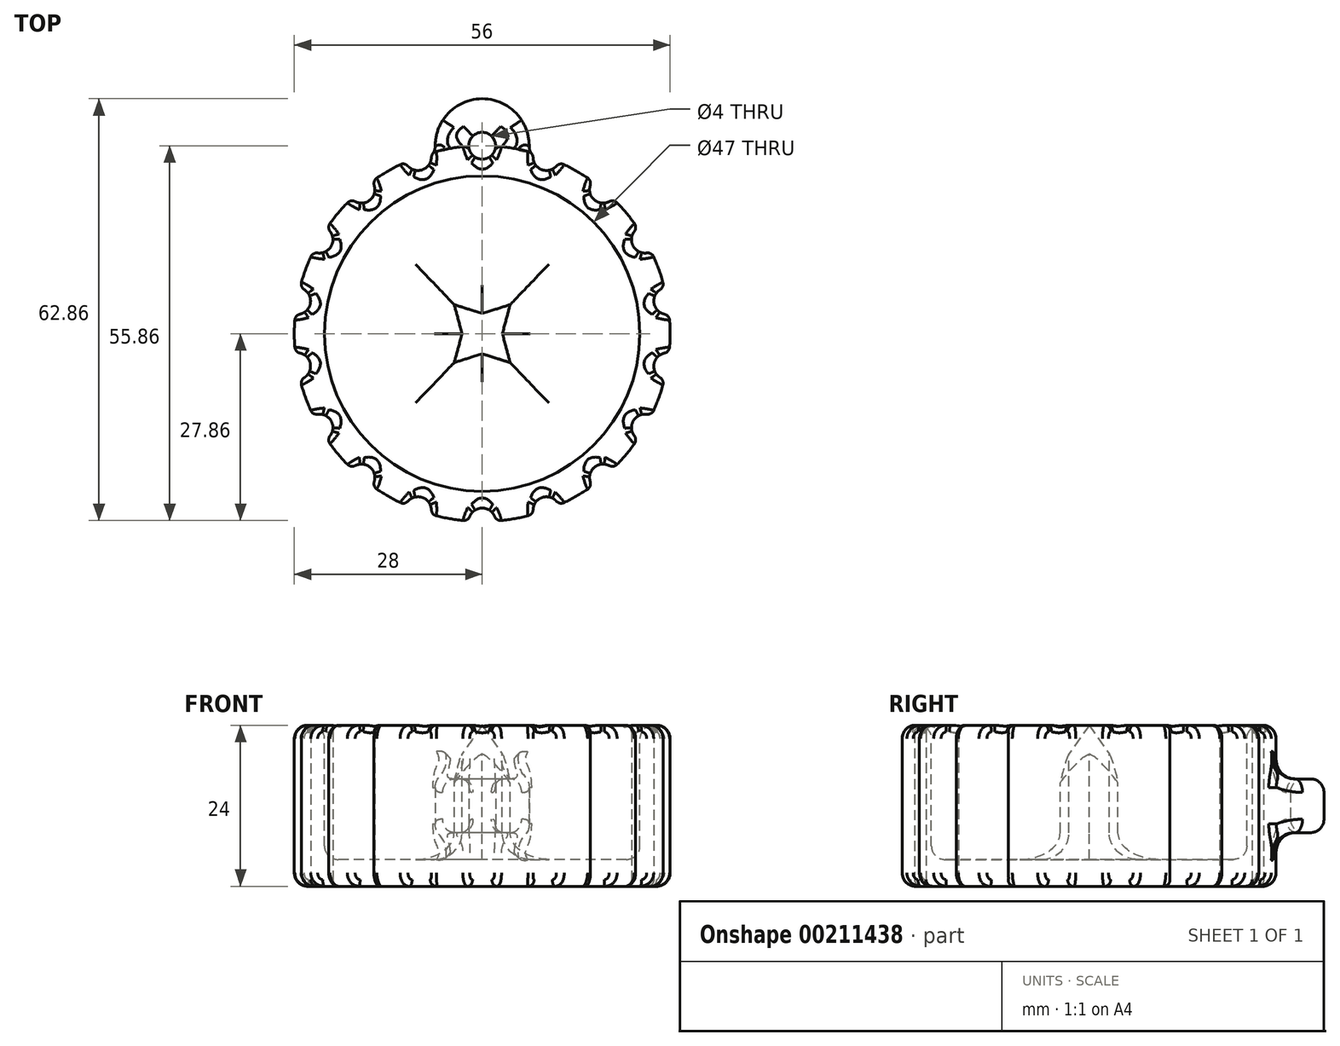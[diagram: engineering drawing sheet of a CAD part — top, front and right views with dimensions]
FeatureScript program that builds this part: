
annotation { "Feature Type Name" : "Feature", "Feature Type Description" : "" }
export const myFeature = defineFeature(function(context is Context, id is Id, definition is map)
    precondition{}
    {
        {
            var Q0;
            Q0=qCreatedBy(makeId("Front.planeOp"),FACE);
            var sketch = newSketch(context, id + "F0", { "sketchPlane" : qUnion([Q0])});
            skLineSegment(sketch, "E0", {"start": v(0, 0) * mm, "end": v(-26, 0) * mm});
            skLineSegment(sketch, "E1", {"start": v(0, 24) * mm, "end": v(0, 0) * mm});
            skLineSegment(sketch, "E2", {"start": v(0, 24) * mm, "end": v(-6, 15.43) * mm});
            skLineSegment(sketch, "E3", {"start": v(-28, 2) * mm, "end": v(-28, 22) * mm});
            skLineSegment(sketch, "E4", {"start": v(-26, 24) * mm, "end": v(-25.5, 24) * mm});
            skPoint(sketch, "E5.visualSharp", {"position": v(-28, 0) * mm});
            skArc(sketch, "E5.filletArc", {"start": v(-28, 2) * mm, "mid": v(-27.41, 0.59) * mm, "end": v(-26, 0) * mm});
            skPoint(sketch, "E6.visualSharp", {"position": v(-28, 24) * mm});
            skArc(sketch, "E6.filletArc", {"start": v(-26, 24) * mm, "mid": v(-27.41, 23.41) * mm, "end": v(-28, 22) * mm});
            skLineSegment(sketch, "E7", {"start": v(-6, 15.43) * mm, "end": v(-6, 4) * mm});
            skLineSegment(sketch, "E8", {"start": v(-23.5, 22) * mm, "end": v(-23.5, 6) * mm});
            skLineSegment(sketch, "E9", {"start": v(-21.5, 4) * mm, "end": v(-6, 4) * mm});
            skPoint(sketch, "E10.visualSharp", {"position": v(-23.5, 4) * mm});
            skArc(sketch, "E10.filletArc", {"start": v(-23.5, 6) * mm, "mid": v(-22.91, 4.59) * mm, "end": v(-21.5, 4) * mm});
            skPoint(sketch, "E11.visualSharp", {"position": v(-23.5, 24) * mm});
            skArc(sketch, "E11.filletArc", {"start": v(-23.5, 22) * mm, "mid": v(-24.09, 23.41) * mm, "end": v(-25.5, 24) * mm});
            skSolve(sketch);
        }
        {
            var Q0;
            Q0=makeQuery(id+"F0.imprint","IMPRINT",FACE,{"disambiguationData":[TD([[makeQuery(id+"F0.imprint","IMPRINT",EDGE,{"derivedFrom":sQuery(id+"F0.wireOp",EDGE,"E0")}),-1.0]])]});
            var Q1;
            Q1=sQuery(id+"F0.wireOp",EDGE,"E1");
            revolve(context, id + "F1", {"entities" : qUnion([Q0]), "axis" : qUnion([Q1]), "revolveType" : RevolveType.FULL});
        }
        {
            var Q0;
            Q0=makeQuery(id+"F1.opRevolve","SWEPT_FACE",FACE,{"disambiguationData":[OSD([sQuery(id+"F0.wireOp",EDGE,"E4")])]});
            var sketch = newSketch(context, id + "F2", { "sketchPlane" : qUnion([Q0])});
            skPoint(sketch, "E12.middle", {"position": v(0, 0) * mm});
            skLineSegment(sketch, "E13.bottom", {"start": v(7.46, 7.46) * mm, "end": v(-7.46, 7.46) * mm});
            skLineSegment(sketch, "E13.top", {"start": v(7.46, -7.46) * mm, "end": v(-7.46, -7.46) * mm});
            skLineSegment(sketch, "E13.left", {"start": v(7.46, 7.46) * mm, "end": v(7.46, -7.46) * mm});
            skLineSegment(sketch, "E13.right", {"start": v(-7.46, 7.46) * mm, "end": v(-7.46, -7.46) * mm});
            skLineSegment(sketch, "E14", {"start": v(-4.17, 4.32) * mm, "end": v(-3, 0) * mm});
            skLineSegment(sketch, "E15", {"start": v(-3, 0) * mm, "end": v(-4.17, -4.32) * mm});
            skLineSegment(sketch, "E16", {"start": v(-4.17, -4.32) * mm, "end": v(0, -3) * mm});
            skLineSegment(sketch, "E17", {"start": v(0, -3) * mm, "end": v(4.17, -4.32) * mm});
            skLineSegment(sketch, "E18", {"start": v(4.17, -4.32) * mm, "end": v(3, 0) * mm});
            skLineSegment(sketch, "E19", {"start": v(3, 0) * mm, "end": v(4.17, 4.32) * mm});
            skLineSegment(sketch, "E20", {"start": v(4.17, 4.32) * mm, "end": v(0, 3) * mm});
            skLineSegment(sketch, "E21", {"start": v(0, 3) * mm, "end": v(-4.17, 4.32) * mm});
            skLineSegment(sketch, "E22", {"start": v(0, -3) * mm, "end": v(0, 0) * mm, "construction": true});
            skLineSegment(sketch, "E23", {"start": v(0, 0) * mm, "end": v(0, 3) * mm, "construction": true});
            skLineSegment(sketch, "E24", {"start": v(-3, 0) * mm, "end": v(0, 0) * mm, "construction": true});
            skLineSegment(sketch, "E25", {"start": v(0, 0) * mm, "end": v(3, 0) * mm, "construction": true});
            skSolve(sketch);
        }
        {
            var Q0;
            Q0=qCreatedBy(makeId("Top.planeOp"),FACE);
            var sketch = newSketch(context, id + "F3", { "sketchPlane" : qUnion([Q0])});
            skCircle(sketch, "E26", {"center": v(0, 28) * mm, "radius": 2 * mm});
            skSolve(sketch);
        }
        {
            var Q0;
            Q0 = qSketchRegion(id + "F3", true);
            extrude(context, id + "F4", {"entities" : qUnion([Q0]), "depth" : 25 * mm});
        }
        {
            var Q0;
            Q0=makeQuery(id+"F4.opExtrude","SWEPT_BODY",BODY,{"disambiguationData":[OSD([sQuery(id+"F3.wireOp",EDGE,"E26")])]});
            var Q1;
            Q1=makeQuery(id+"F1.opRevolve","SWEPT_FACE",FACE,{"disambiguationData":[OSD([sQuery(id+"F0.wireOp",EDGE,"E6.filletArc")])]});
            circularPattern(context, id + "F5", {"entities" : qUnion([Q0]), "axis" : qUnion([Q1]), "angle" : 360 * degree, "instanceCount" : 18, "equalSpace" : true});
        }
        {
            var Q0;
            Q0=makeQuery(id+"F5.opPattern","COPY",BODY,{"derivedFrom":makeQuery(id+"F4.opExtrude","SWEPT_BODY",BODY,{"disambiguationData":[OSD([sQuery(id+"F3.wireOp",EDGE,"E26")])]}),"instanceName":"1"});
            var Q1;
            Q1=makeQuery(id+"F4.opExtrude","SWEPT_BODY",BODY,{"disambiguationData":[OSD([sQuery(id+"F3.wireOp",EDGE,"E26")])]});
            var Q2;
            Q2=makeQuery(id+"F5.opPattern","COPY",BODY,{"derivedFrom":makeQuery(id+"F4.opExtrude","SWEPT_BODY",BODY,{"disambiguationData":[OSD([sQuery(id+"F3.wireOp",EDGE,"E26")])]}),"instanceName":"17"});
            var Q3;
            Q3=makeQuery(id+"F5.opPattern","COPY",BODY,{"derivedFrom":makeQuery(id+"F4.opExtrude","SWEPT_BODY",BODY,{"disambiguationData":[OSD([sQuery(id+"F3.wireOp",EDGE,"E26")])]}),"instanceName":"16"});
            var Q4;
            Q4=makeQuery(id+"F5.opPattern","COPY",BODY,{"derivedFrom":makeQuery(id+"F4.opExtrude","SWEPT_BODY",BODY,{"disambiguationData":[OSD([sQuery(id+"F3.wireOp",EDGE,"E26")])]}),"instanceName":"15"});
            var Q5;
            Q5=makeQuery(id+"F5.opPattern","COPY",BODY,{"derivedFrom":makeQuery(id+"F4.opExtrude","SWEPT_BODY",BODY,{"disambiguationData":[OSD([sQuery(id+"F3.wireOp",EDGE,"E26")])]}),"instanceName":"14"});
            var Q6;
            Q6=makeQuery(id+"F5.opPattern","COPY",BODY,{"derivedFrom":makeQuery(id+"F4.opExtrude","SWEPT_BODY",BODY,{"disambiguationData":[OSD([sQuery(id+"F3.wireOp",EDGE,"E26")])]}),"instanceName":"13"});
            var Q7;
            Q7=makeQuery(id+"F5.opPattern","COPY",BODY,{"derivedFrom":makeQuery(id+"F4.opExtrude","SWEPT_BODY",BODY,{"disambiguationData":[OSD([sQuery(id+"F3.wireOp",EDGE,"E26")])]}),"instanceName":"12"});
            var Q8;
            Q8=makeQuery(id+"F5.opPattern","COPY",BODY,{"derivedFrom":makeQuery(id+"F4.opExtrude","SWEPT_BODY",BODY,{"disambiguationData":[OSD([sQuery(id+"F3.wireOp",EDGE,"E26")])]}),"instanceName":"11"});
            var Q9;
            Q9=makeQuery(id+"F5.opPattern","COPY",BODY,{"derivedFrom":makeQuery(id+"F4.opExtrude","SWEPT_BODY",BODY,{"disambiguationData":[OSD([sQuery(id+"F3.wireOp",EDGE,"E26")])]}),"instanceName":"10"});
            var Q10;
            Q10=makeQuery(id+"F5.opPattern","COPY",BODY,{"derivedFrom":makeQuery(id+"F4.opExtrude","SWEPT_BODY",BODY,{"disambiguationData":[OSD([sQuery(id+"F3.wireOp",EDGE,"E26")])]}),"instanceName":"9"});
            var Q11;
            Q11=makeQuery(id+"F5.opPattern","COPY",BODY,{"derivedFrom":makeQuery(id+"F4.opExtrude","SWEPT_BODY",BODY,{"disambiguationData":[OSD([sQuery(id+"F3.wireOp",EDGE,"E26")])]}),"instanceName":"8"});
            var Q12;
            Q12=makeQuery(id+"F5.opPattern","COPY",BODY,{"derivedFrom":makeQuery(id+"F4.opExtrude","SWEPT_BODY",BODY,{"disambiguationData":[OSD([sQuery(id+"F3.wireOp",EDGE,"E26")])]}),"instanceName":"7"});
            var Q13;
            Q13=makeQuery(id+"F5.opPattern","COPY",BODY,{"derivedFrom":makeQuery(id+"F4.opExtrude","SWEPT_BODY",BODY,{"disambiguationData":[OSD([sQuery(id+"F3.wireOp",EDGE,"E26")])]}),"instanceName":"6"});
            var Q14;
            Q14=makeQuery(id+"F5.opPattern","COPY",BODY,{"derivedFrom":makeQuery(id+"F4.opExtrude","SWEPT_BODY",BODY,{"disambiguationData":[OSD([sQuery(id+"F3.wireOp",EDGE,"E26")])]}),"instanceName":"5"});
            var Q15;
            Q15=makeQuery(id+"F5.opPattern","COPY",BODY,{"derivedFrom":makeQuery(id+"F4.opExtrude","SWEPT_BODY",BODY,{"disambiguationData":[OSD([sQuery(id+"F3.wireOp",EDGE,"E26")])]}),"instanceName":"4"});
            var Q16;
            Q16=makeQuery(id+"F5.opPattern","COPY",BODY,{"derivedFrom":makeQuery(id+"F4.opExtrude","SWEPT_BODY",BODY,{"disambiguationData":[OSD([sQuery(id+"F3.wireOp",EDGE,"E26")])]}),"instanceName":"3"});
            var Q17;
            Q17=makeQuery(id+"F5.opPattern","COPY",BODY,{"derivedFrom":makeQuery(id+"F4.opExtrude","SWEPT_BODY",BODY,{"disambiguationData":[OSD([sQuery(id+"F3.wireOp",EDGE,"E26")])]}),"instanceName":"2"});
            var Q18;
            Q18=makeQuery(id+"F1.opRevolve","SWEPT_BODY",BODY,{"disambiguationData":[OSD([sQuery(id+"F0.wireOp",EDGE,"E0"),sQuery(id+"F0.wireOp",EDGE,"LKls2v4x-rZpt-SCUw-E1KC-NKs2JK7PPKrY"),sQuery(id+"F0.wireOp",EDGE,"E1"),sQuery(id+"F0.wireOp",EDGE,"Zr3oMY1M-Fj8H-FIV4-PLXo-I462BJgf3CWp"),sQuery(id+"F0.wireOp",EDGE,"iYLJxYrQ-jAf5-QbV3-Oahl-a6r2LaxN3Rx7"),sQuery(id+"F0.wireOp",EDGE,"E2"),sQuery(id+"F0.wireOp",EDGE,"uqPazPdR-SNv0-wGVJ-T0MR-8ju2Ulaitwt3"),sQuery(id+"F0.wireOp",EDGE,"7kJ7LNRW-MLzO-1vut-xwnV-VTICPbpiV8Su")])]});
            booleanBodies(context, id + "F6", {"operationType" : BooleanOperationType.SUBTRACTION, "tools" : qUnion([Q0, Q1, Q2, Q3, Q4, Q5, Q6, Q7, Q8, Q9, Q10, Q11, Q12, Q13, Q14, Q15, Q16, Q17]), "targets" : qUnion([Q18])});
        }
        {
            var Q0;
            Q0=makeQuery(id+"F6.opBoolean","COPY",FACE,{"derivedFrom":makeQuery(id+"F5.opPattern","COPY",FACE,{"derivedFrom":makeQuery(id+"F4.opExtrude","SWEPT_FACE",FACE,{"disambiguationData":[OSD([sQuery(id+"F3.wireOp",EDGE,"E26")])]}),"instanceName":"10"})});
            var Q1;
            Q1=makeQuery(id+"F6.opBoolean","COPY",FACE,{"derivedFrom":makeQuery(id+"F5.opPattern","COPY",FACE,{"derivedFrom":makeQuery(id+"F4.opExtrude","SWEPT_FACE",FACE,{"disambiguationData":[OSD([sQuery(id+"F3.wireOp",EDGE,"E26")])]}),"instanceName":"11"})});
            var Q2;
            Q2=makeQuery(id+"F6.opBoolean","COPY",FACE,{"derivedFrom":makeQuery(id+"F5.opPattern","COPY",FACE,{"derivedFrom":makeQuery(id+"F4.opExtrude","SWEPT_FACE",FACE,{"disambiguationData":[OSD([sQuery(id+"F3.wireOp",EDGE,"E26")])]}),"instanceName":"12"})});
            var Q3;
            Q3=makeQuery(id+"F6.opBoolean","COPY",FACE,{"derivedFrom":makeQuery(id+"F5.opPattern","COPY",FACE,{"derivedFrom":makeQuery(id+"F4.opExtrude","SWEPT_FACE",FACE,{"disambiguationData":[OSD([sQuery(id+"F3.wireOp",EDGE,"E26")])]}),"instanceName":"13"})});
            var Q4;
            Q4=makeQuery(id+"F6.opBoolean","COPY",FACE,{"derivedFrom":makeQuery(id+"F5.opPattern","COPY",FACE,{"derivedFrom":makeQuery(id+"F4.opExtrude","SWEPT_FACE",FACE,{"disambiguationData":[OSD([sQuery(id+"F3.wireOp",EDGE,"E26")])]}),"instanceName":"14"})});
            var Q5;
            Q5=makeQuery(id+"F6.opBoolean","COPY",FACE,{"derivedFrom":makeQuery(id+"F5.opPattern","COPY",FACE,{"derivedFrom":makeQuery(id+"F4.opExtrude","SWEPT_FACE",FACE,{"disambiguationData":[OSD([sQuery(id+"F3.wireOp",EDGE,"E26")])]}),"instanceName":"15"})});
            var Q6;
            Q6=makeQuery(id+"F6.opBoolean","COPY",FACE,{"derivedFrom":makeQuery(id+"F5.opPattern","COPY",FACE,{"derivedFrom":makeQuery(id+"F4.opExtrude","SWEPT_FACE",FACE,{"disambiguationData":[OSD([sQuery(id+"F3.wireOp",EDGE,"E26")])]}),"instanceName":"16"})});
            var Q7;
            Q7=makeQuery(id+"F6.opBoolean","COPY",FACE,{"derivedFrom":makeQuery(id+"F5.opPattern","COPY",FACE,{"derivedFrom":makeQuery(id+"F4.opExtrude","SWEPT_FACE",FACE,{"disambiguationData":[OSD([sQuery(id+"F3.wireOp",EDGE,"E26")])]}),"instanceName":"17"})});
            var Q8;
            Q8=makeQuery(id+"F6.opBoolean","COPY",FACE,{"derivedFrom":makeQuery(id+"F4.opExtrude","SWEPT_FACE",FACE,{"disambiguationData":[OSD([sQuery(id+"F3.wireOp",EDGE,"E26")])]})});
            var Q9;
            Q9=makeQuery(id+"F6.opBoolean","COPY",FACE,{"derivedFrom":makeQuery(id+"F5.opPattern","COPY",FACE,{"derivedFrom":makeQuery(id+"F4.opExtrude","SWEPT_FACE",FACE,{"disambiguationData":[OSD([sQuery(id+"F3.wireOp",EDGE,"E26")])]}),"instanceName":"1"})});
            var Q10;
            Q10=makeQuery(id+"F6.opBoolean","COPY",FACE,{"derivedFrom":makeQuery(id+"F5.opPattern","COPY",FACE,{"derivedFrom":makeQuery(id+"F4.opExtrude","SWEPT_FACE",FACE,{"disambiguationData":[OSD([sQuery(id+"F3.wireOp",EDGE,"E26")])]}),"instanceName":"2"})});
            var Q11;
            Q11=makeQuery(id+"F6.opBoolean","COPY",FACE,{"derivedFrom":makeQuery(id+"F5.opPattern","COPY",FACE,{"derivedFrom":makeQuery(id+"F4.opExtrude","SWEPT_FACE",FACE,{"disambiguationData":[OSD([sQuery(id+"F3.wireOp",EDGE,"E26")])]}),"instanceName":"3"})});
            var Q12;
            Q12=makeQuery(id+"F6.opBoolean","COPY",FACE,{"derivedFrom":makeQuery(id+"F5.opPattern","COPY",FACE,{"derivedFrom":makeQuery(id+"F4.opExtrude","SWEPT_FACE",FACE,{"disambiguationData":[OSD([sQuery(id+"F3.wireOp",EDGE,"E26")])]}),"instanceName":"4"})});
            var Q13;
            Q13=makeQuery(id+"F6.opBoolean","COPY",FACE,{"derivedFrom":makeQuery(id+"F5.opPattern","COPY",FACE,{"derivedFrom":makeQuery(id+"F4.opExtrude","SWEPT_FACE",FACE,{"disambiguationData":[OSD([sQuery(id+"F3.wireOp",EDGE,"E26")])]}),"instanceName":"5"})});
            var Q14;
            Q14=makeQuery(id+"F6.opBoolean","COPY",FACE,{"derivedFrom":makeQuery(id+"F5.opPattern","COPY",FACE,{"derivedFrom":makeQuery(id+"F4.opExtrude","SWEPT_FACE",FACE,{"disambiguationData":[OSD([sQuery(id+"F3.wireOp",EDGE,"E26")])]}),"instanceName":"6"})});
            var Q15;
            Q15=makeQuery(id+"F6.opBoolean","COPY",FACE,{"derivedFrom":makeQuery(id+"F5.opPattern","COPY",FACE,{"derivedFrom":makeQuery(id+"F4.opExtrude","SWEPT_FACE",FACE,{"disambiguationData":[OSD([sQuery(id+"F3.wireOp",EDGE,"E26")])]}),"instanceName":"7"})});
            var Q16;
            Q16=makeQuery(id+"F6.opBoolean","COPY",FACE,{"derivedFrom":makeQuery(id+"F5.opPattern","COPY",FACE,{"derivedFrom":makeQuery(id+"F4.opExtrude","SWEPT_FACE",FACE,{"disambiguationData":[OSD([sQuery(id+"F3.wireOp",EDGE,"E26")])]}),"instanceName":"8"})});
            var Q17;
            Q17=makeQuery(id+"F6.opBoolean","COPY",FACE,{"derivedFrom":makeQuery(id+"F5.opPattern","COPY",FACE,{"derivedFrom":makeQuery(id+"F4.opExtrude","SWEPT_FACE",FACE,{"disambiguationData":[OSD([sQuery(id+"F3.wireOp",EDGE,"E26")])]}),"instanceName":"9"})});
            fillet(context, id + "F7", {"entities" : qUnion([Q0, Q1, Q2, Q3, Q4, Q5, Q6, Q7, Q8, Q9, Q10, Q11, Q12, Q13, Q14, Q15, Q16, Q17]), "radius" : 1 * mm, "tangentPropagation" : true, "allowEdgeOverflow" : false});
        }
        {
            var Q0;
            Q0 = qSketchRegion(id + "F2", true);
            extrude(context, id + "F8", {"entities" : qUnion([Q0]), "operationType" : NewBodyOperationType.REMOVE, "oppositeDirection" : true, "depth" : 20 * mm});
        }
        {
            var Q0;
            Q0=makeQuery(id+"F8.boolean.opBoolean","MERGE",FACE,{"derivedFrom":[makeQuery(id+"F1.opRevolve","SWEPT_FACE",FACE,{"disambiguationData":[OSD([sQuery(id+"F0.wireOp",EDGE,"E9")])]}),makeQuery(id+"F8.opExtrude","CAP_FACE",FACE,{"disambiguationData":[OSD([sQuery(id+"F2.wireOp",EDGE,"E13.bottom"),sQuery(id+"F2.wireOp",EDGE,"E13.top"),sQuery(id+"F2.wireOp",EDGE,"E13.left"),sQuery(id+"F2.wireOp",EDGE,"E13.right"),sQuery(id+"F2.wireOp",EDGE,"E14"),sQuery(id+"F2.wireOp",EDGE,"E15"),sQuery(id+"F2.wireOp",EDGE,"E16"),sQuery(id+"F2.wireOp",EDGE,"E17"),sQuery(id+"F2.wireOp",EDGE,"E18"),sQuery(id+"F2.wireOp",EDGE,"E19"),sQuery(id+"F2.wireOp",EDGE,"E20"),sQuery(id+"F2.wireOp",EDGE,"E21")])],"isStart":false})]});
            fillet(context, id + "F9", {"entities" : qUnion([Q0]), "radius" : 4 * mm, "tangentPropagation" : true, "allowEdgeOverflow" : false});
        }
        {
            var Q0;
            Q0=qCreatedBy(makeId("Top.planeOp"),FACE);
            var sketch = newSketch(context, id + "F10", { "sketchPlane" : qUnion([Q0])});
            skArc(sketch, "E27", {"start": v(6.86, 26.63) * mm, "mid": v(0, 35) * mm, "end": v(-6.86, 26.63) * mm});
            skArc(sketch, "E28", {"start": v(1.46, 26.63) * mm, "mid": v(0, 30) * mm, "end": v(-1.46, 26.63) * mm});
            skPoint(sketch, "E29", {"position": v(-1.46, 26.63) * mm});
            skPoint(sketch, "E30", {"position": v(-6.86, 26.63) * mm});
            skPoint(sketch, "E31", {"position": v(1.46, 26.63) * mm});
            skPoint(sketch, "E32", {"position": v(6.86, 26.63) * mm});
            skLineSegment(sketch, "E33", {"start": v(6.86, 26.63) * mm, "end": v(1.46, 26.63) * mm});
            skLineSegment(sketch, "E34", {"start": v(-1.46, 26.63) * mm, "end": v(-6.86, 26.63) * mm});
            skSolve(sketch);
        }
        {
            var Q0;
            Q0=makeQuery(id+"F10.imprint","IMPRINT",FACE,{"disambiguationData":[TD([[makeQuery(id+"F10.imprint","IMPRINT",EDGE,{"derivedFrom":sQuery(id+"F10.wireOp",EDGE,"E27")}),1.0]])]});
            extrude(context, id + "F11", {"entities" : qUnion([Q0]), "depth" : 8 * mm});
        }
        {
            var Q0;
            Q0=makeQuery(id+"F11.opExtrude","SWEPT_BODY",BODY,{"disambiguationData":[OSD([sQuery(id+"F10.wireOp",EDGE,"E27"),sQuery(id+"F10.wireOp",EDGE,"E28"),sQuery(id+"F10.wireOp",EDGE,"E33"),sQuery(id+"F10.wireOp",EDGE,"E34")])]});
            var Q1;
            Q1=makeQuery(id+"F6.opBoolean","COPY",FACE,{"derivedFrom":makeQuery(id+"F4.opExtrude","SWEPT_FACE",FACE,{"disambiguationData":[OSD([sQuery(id+"F3.wireOp",EDGE,"E26")])]})});
            transform(context, id + "F12", {"entities" : qUnion([Q0]), "transformType" : TransformType.TRANSLATION_DISTANCE, "transformDirection" : qUnion([Q1]), "distance" : 8 * mm, "makeCopy" : false});
        }
        {
            var Q0;
            Q0=makeQuery(id+"F11.opExtrude","SWEPT_BODY",BODY,{"disambiguationData":[OSD([sQuery(id+"F10.wireOp",EDGE,"E27"),sQuery(id+"F10.wireOp",EDGE,"E28"),sQuery(id+"F10.wireOp",EDGE,"E33"),sQuery(id+"F10.wireOp",EDGE,"E34")])]});
            var Q1;
            Q1=makeQuery(id+"F1.opRevolve","SWEPT_BODY",BODY,{"disambiguationData":[OSD([sQuery(id+"F0.wireOp",EDGE,"E0"),sQuery(id+"F0.wireOp",EDGE,"E1"),sQuery(id+"F0.wireOp",EDGE,"E2"),sQuery(id+"F0.wireOp",EDGE,"E3"),sQuery(id+"F0.wireOp",EDGE,"E4"),sQuery(id+"F0.wireOp",EDGE,"E5.filletArc"),sQuery(id+"F0.wireOp",EDGE,"E6.filletArc"),sQuery(id+"F0.wireOp",EDGE,"E7"),sQuery(id+"F0.wireOp",EDGE,"E8"),sQuery(id+"F0.wireOp",EDGE,"E9"),sQuery(id+"F0.wireOp",EDGE,"E10.filletArc"),sQuery(id+"F0.wireOp",EDGE,"E11.filletArc")])]});
            booleanBodies(context, id + "F13", {"operationType" : BooleanOperationType.UNION, "tools" : qUnion([Q0, Q1])});
        }
        {
            var Q0;
            {var subQ0=makeQuery(id+"F4.opExtrude","SWEPT_FACE",FACE,{"disambiguationData":[OSD([sQuery(id+"F3.wireOp",EDGE,"E26")])]});Q0=makeQuery(id+"F13.opBoolean","INTERSECT",EDGE,{"derivedFrom":[makeQuery(id+"F6.opBoolean","SPLIT",FACE,{"disambiguationData":[TD([makeQuery(id+"F1.opRevolve","SWEPT_FACE",FACE,{"disambiguationData":[OSD([sQuery(id+"F0.wireOp",EDGE,"E5.filletArc")])]}),makeQuery(id+"F1.opRevolve","SWEPT_FACE",FACE,{"disambiguationData":[OSD([sQuery(id+"F0.wireOp",EDGE,"E6.filletArc")])]}),subQ0,makeQuery(id+"F5.opPattern","COPY",FACE,{"derivedFrom":subQ0,"instanceName":"17"})])],"derivedFrom":makeQuery(id+"F1.opRevolve","SWEPT_FACE",FACE,{"disambiguationData":[OSD([sQuery(id+"F0.wireOp",EDGE,"E3")])]})}),makeQuery(id+"F11.opExtrude","CAP_FACE",FACE,{"disambiguationData":[OSD([sQuery(id+"F10.wireOp",EDGE,"E27"),sQuery(id+"F10.wireOp",EDGE,"E28"),sQuery(id+"F10.wireOp",EDGE,"E33"),sQuery(id+"F10.wireOp",EDGE,"E34")])],"isStart":true})]});}
            var Q1;
            {var subQ0=makeQuery(id+"F4.opExtrude","SWEPT_FACE",FACE,{"disambiguationData":[OSD([sQuery(id+"F3.wireOp",EDGE,"E26")])]});Q1=makeQuery(id+"F13.opBoolean","INTERSECT",EDGE,{"derivedFrom":[makeQuery(id+"F6.opBoolean","SPLIT",FACE,{"disambiguationData":[TD([makeQuery(id+"F1.opRevolve","SWEPT_FACE",FACE,{"disambiguationData":[OSD([sQuery(id+"F0.wireOp",EDGE,"E5.filletArc")])]}),makeQuery(id+"F1.opRevolve","SWEPT_FACE",FACE,{"disambiguationData":[OSD([sQuery(id+"F0.wireOp",EDGE,"E6.filletArc")])]}),subQ0,makeQuery(id+"F5.opPattern","COPY",FACE,{"derivedFrom":subQ0,"instanceName":"1"})])],"derivedFrom":makeQuery(id+"F1.opRevolve","SWEPT_FACE",FACE,{"disambiguationData":[OSD([sQuery(id+"F0.wireOp",EDGE,"E3")])]})}),makeQuery(id+"F11.opExtrude","CAP_FACE",FACE,{"disambiguationData":[OSD([sQuery(id+"F10.wireOp",EDGE,"E27"),sQuery(id+"F10.wireOp",EDGE,"E28"),sQuery(id+"F10.wireOp",EDGE,"E33"),sQuery(id+"F10.wireOp",EDGE,"E34")])],"isStart":true})]});}
            var Q2;
            {var subQ0=makeQuery(id+"F4.opExtrude","SWEPT_FACE",FACE,{"disambiguationData":[OSD([sQuery(id+"F3.wireOp",EDGE,"E26")])]});Q2=makeQuery(id+"F13.opBoolean","INTERSECT",EDGE,{"derivedFrom":[makeQuery(id+"F6.opBoolean","SPLIT",FACE,{"disambiguationData":[TD([makeQuery(id+"F1.opRevolve","SWEPT_FACE",FACE,{"disambiguationData":[OSD([sQuery(id+"F0.wireOp",EDGE,"E5.filletArc")])]}),makeQuery(id+"F1.opRevolve","SWEPT_FACE",FACE,{"disambiguationData":[OSD([sQuery(id+"F0.wireOp",EDGE,"E6.filletArc")])]}),subQ0,makeQuery(id+"F5.opPattern","COPY",FACE,{"derivedFrom":subQ0,"instanceName":"1"})])],"derivedFrom":makeQuery(id+"F1.opRevolve","SWEPT_FACE",FACE,{"disambiguationData":[OSD([sQuery(id+"F0.wireOp",EDGE,"E3")])]})}),makeQuery(id+"F11.opExtrude","CAP_FACE",FACE,{"disambiguationData":[OSD([sQuery(id+"F10.wireOp",EDGE,"E27"),sQuery(id+"F10.wireOp",EDGE,"E28"),sQuery(id+"F10.wireOp",EDGE,"E33"),sQuery(id+"F10.wireOp",EDGE,"E34")])],"isStart":false})]});}
            var Q3;
            {var subQ0=makeQuery(id+"F4.opExtrude","SWEPT_FACE",FACE,{"disambiguationData":[OSD([sQuery(id+"F3.wireOp",EDGE,"E26")])]});Q3=makeQuery(id+"F13.opBoolean","INTERSECT",EDGE,{"derivedFrom":[makeQuery(id+"F6.opBoolean","SPLIT",FACE,{"disambiguationData":[TD([makeQuery(id+"F1.opRevolve","SWEPT_FACE",FACE,{"disambiguationData":[OSD([sQuery(id+"F0.wireOp",EDGE,"E5.filletArc")])]}),makeQuery(id+"F1.opRevolve","SWEPT_FACE",FACE,{"disambiguationData":[OSD([sQuery(id+"F0.wireOp",EDGE,"E6.filletArc")])]}),subQ0,makeQuery(id+"F5.opPattern","COPY",FACE,{"derivedFrom":subQ0,"instanceName":"17"})])],"derivedFrom":makeQuery(id+"F1.opRevolve","SWEPT_FACE",FACE,{"disambiguationData":[OSD([sQuery(id+"F0.wireOp",EDGE,"E3")])]})}),makeQuery(id+"F11.opExtrude","CAP_FACE",FACE,{"disambiguationData":[OSD([sQuery(id+"F10.wireOp",EDGE,"E27"),sQuery(id+"F10.wireOp",EDGE,"E28"),sQuery(id+"F10.wireOp",EDGE,"E33"),sQuery(id+"F10.wireOp",EDGE,"E34")])],"isStart":false})]});}
            fillet(context, id + "F14", {"entities" : qUnion([Q0, Q1, Q2, Q3]), "radius" : 3 * mm, "tangentPropagation" : true, "allowEdgeOverflow" : false});
        }
        {
            var Q0;
            Q0=makeQuery(id+"F11.opExtrude","CAP_FACE",FACE,{"disambiguationData":[OSD([sQuery(id+"F10.wireOp",EDGE,"E27"),sQuery(id+"F10.wireOp",EDGE,"E28"),sQuery(id+"F10.wireOp",EDGE,"E33"),sQuery(id+"F10.wireOp",EDGE,"E34")])],"isStart":false});
            var Q1;
            Q1=makeQuery(id+"F11.opExtrude","CAP_FACE",FACE,{"disambiguationData":[OSD([sQuery(id+"F10.wireOp",EDGE,"E27"),sQuery(id+"F10.wireOp",EDGE,"E28"),sQuery(id+"F10.wireOp",EDGE,"E33"),sQuery(id+"F10.wireOp",EDGE,"E34")])],"isStart":true});
            fillet(context, id + "F15", {"entities" : qUnion([Q0, Q1]), "radius" : 2 * mm, "tangentPropagation" : true, "allowEdgeOverflow" : false});
        }
        {
            var Q0;
            Q0=makeQuery(id+"F11.opExtrude","SWEPT_FACE",FACE,{"disambiguationData":[OSD([sQuery(id+"F10.wireOp",EDGE,"E27")])]});
            fillet(context, id + "F16", {"entities" : qUnion([Q0]), "radius" : 2 * mm, "tangentPropagation" : true, "allowEdgeOverflow" : false});
        }
    });
